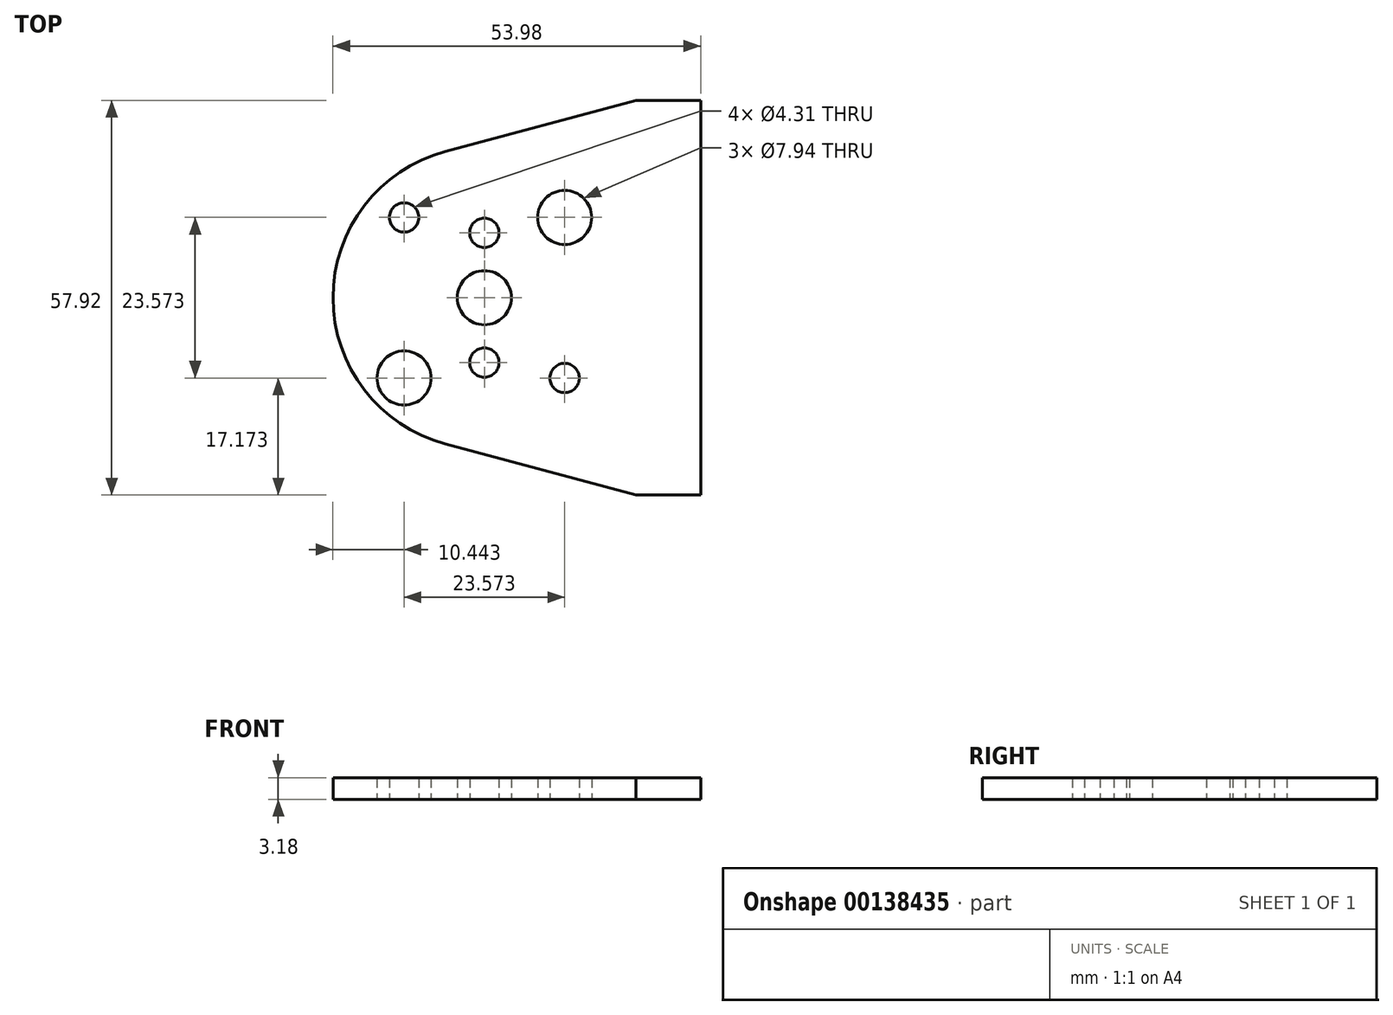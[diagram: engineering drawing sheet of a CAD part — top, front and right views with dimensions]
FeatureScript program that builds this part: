
annotation { "Feature Type Name" : "Feature", "Feature Type Description" : "" }
export const myFeature = defineFeature(function(context is Context, id is Id, definition is map)
    precondition{}
    {
        {
            var Q0;
            Q0=qCreatedBy(makeId("Top.planeOp"),FACE);
            var sketch = newSketch(context, id + "F0", { "sketchPlane" : qUnion([Q0])});
            skCircle(sketch, "E0", {"center": v(0, 0) * mm, "radius": 3.97 * mm});
            skLineSegment(sketch, "E1.bottom", {"start": v(-11.79, 11.79) * mm, "end": v(11.79, 11.79) * mm, "construction": true});
            skLineSegment(sketch, "E1.top", {"start": v(-11.79, -11.79) * mm, "end": v(11.79, -11.79) * mm, "construction": true});
            skLineSegment(sketch, "E1.left", {"start": v(-11.79, 11.79) * mm, "end": v(-11.79, -11.79) * mm, "construction": true});
            skLineSegment(sketch, "E1.right", {"start": v(11.79, 11.79) * mm, "end": v(11.79, -11.79) * mm, "construction": true});
            skCircle(sketch, "E2", {"center": v(0, 0) * mm, "radius": 11.11 * mm, "construction": true});
            skCircle(sketch, "E3", {"center": v(-11.79, 11.79) * mm, "radius": 5.56 * mm, "construction": true});
            skCircle(sketch, "E4", {"center": v(-11.79, 11.79) * mm, "radius": 2.15 * mm});
            skCircle(sketch, "E5", {"center": v(11.79, 11.79) * mm, "radius": 3.97 * mm});
            skCircle(sketch, "E6", {"center": v(-11.79, -11.79) * mm, "radius": 3.97 * mm});
            skCircle(sketch, "E7", {"center": v(11.79, -11.79) * mm, "radius": 2.15 * mm});
            skLineSegment(sketch, "E8", {"start": v(0, 0) * mm, "end": v(22.23, 0) * mm, "construction": true});
            skLineSegment(sketch, "E9.bottom", {"start": v(22.23, 28.96) * mm, "end": v(31.75, 28.96) * mm});
            skLineSegment(sketch, "E9.top", {"start": v(22.23, -28.96) * mm, "end": v(31.75, -28.96) * mm});
            skLineSegment(sketch, "E9.left", {"start": v(22.23, 28.96) * mm, "end": v(22.23, -28.96) * mm, "construction": true});
            skLineSegment(sketch, "E9.right", {"start": v(31.75, 28.96) * mm, "end": v(31.75, -28.96) * mm});
            skArc(sketch, "E10", {"start": v(-5.75, 21.47) * mm, "mid": v(-22.22, 0) * mm, "end": v(-5.75, -21.47) * mm});
            skLineSegment(sketch, "E11", {"start": v(-5.75, 21.47) * mm, "end": v(22.23, 28.96) * mm});
            skLineSegment(sketch, "E12", {"start": v(-5.75, -21.47) * mm, "end": v(22.23, -28.96) * mm});
            skLineSegment(sketch, "E13", {"start": v(-5.75, 21.47) * mm, "end": v(8.24, 21.47) * mm, "construction": true});
            skLineSegment(sketch, "E14", {"start": v(8.24, 21.47) * mm, "end": v(8.24, 25.22) * mm, "construction": true});
            skLineSegment(sketch, "E15", {"start": v(0, 9.53) * mm, "end": v(0, -9.53) * mm, "construction": true});
            skCircle(sketch, "E16", {"center": v(0, 9.53) * mm, "radius": 2.15 * mm});
            skCircle(sketch, "E17", {"center": v(0, -9.53) * mm, "radius": 2.15 * mm});
            skSolve(sketch);
        }
        {
            var Q0;
            Q0 = qSketchRegion(id + "F0", true);
            extrude(context, id + "F1", {"entities" : qUnion([Q0]), "depth" : 3.17 * mm});
        }
    });
